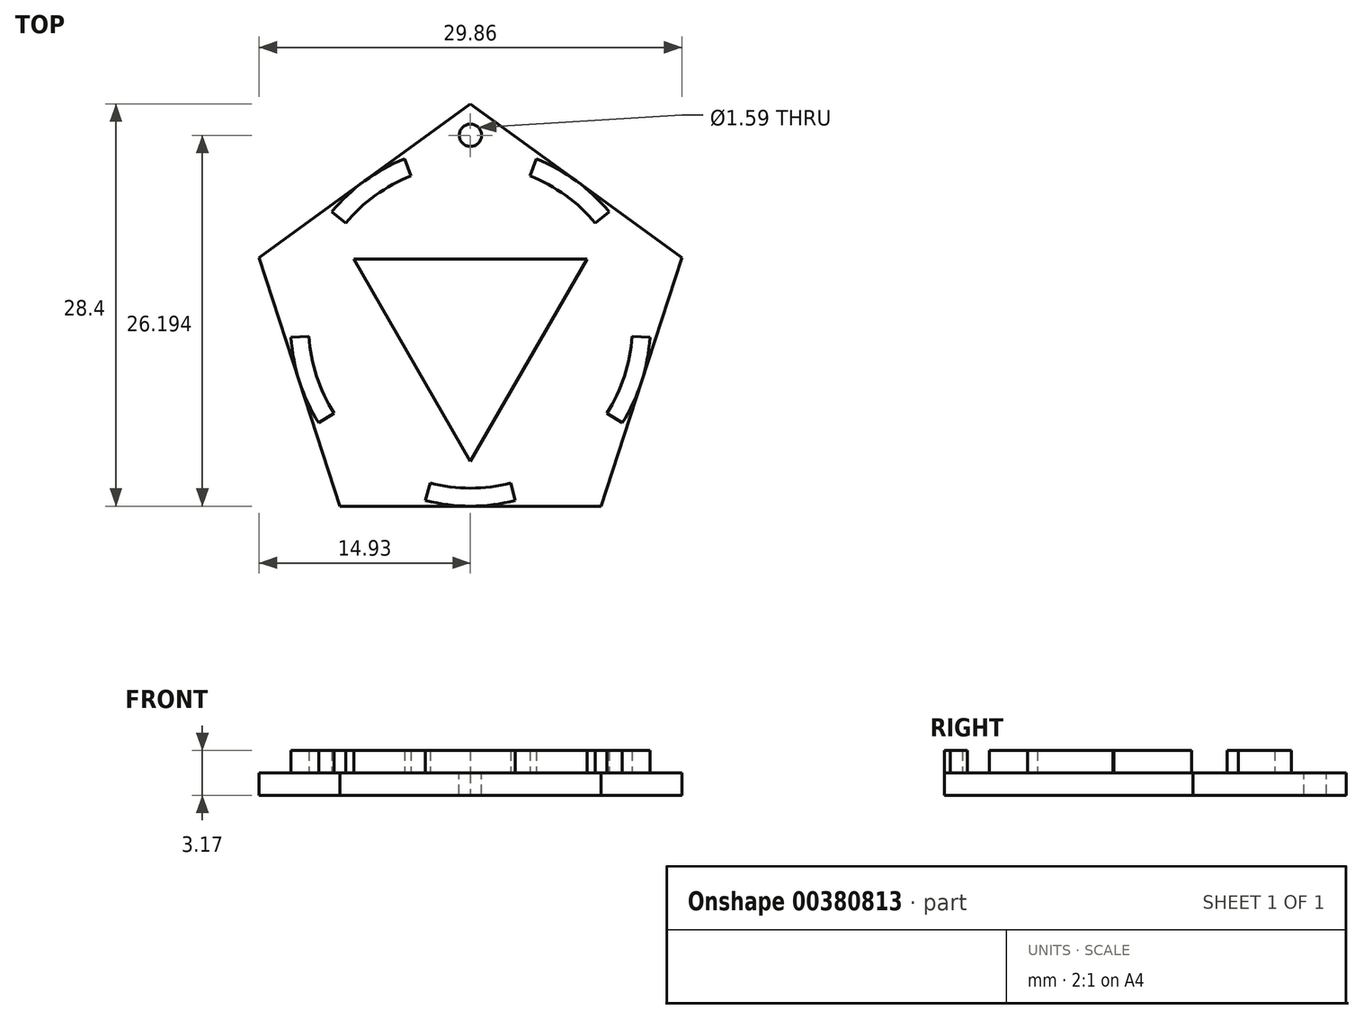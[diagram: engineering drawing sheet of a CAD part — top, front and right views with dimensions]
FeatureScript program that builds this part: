
annotation { "Feature Type Name" : "Feature", "Feature Type Description" : "" }
export const myFeature = defineFeature(function(context is Context, id is Id, definition is map)
    precondition{}
    {
        {
            var Q0;
            Q0=qCreatedBy(makeId("Top.planeOp"),FACE);
            var sketch = newSketch(context, id + "F0", { "sketchPlane" : qUnion([Q0])});
            skCircle(sketch, "E0.cCircle", {"center": v(0, 0) * mm, "radius": 12.7 * mm, "construction": true});
            skLineSegment(sketch, "E0.0", {"start": v(-9.23, -12.7) * mm, "end": v(9.23, -12.7) * mm});
            skLineSegment(sketch, "E0.1", {"start": v(-14.93, 4.85) * mm, "end": v(-9.23, -12.7) * mm});
            skLineSegment(sketch, "E0.2", {"start": v(0, 15.7) * mm, "end": v(-14.93, 4.85) * mm});
            skLineSegment(sketch, "E0.3", {"start": v(14.93, 4.85) * mm, "end": v(0, 15.7) * mm});
            skLineSegment(sketch, "E0.4", {"start": v(9.23, -12.7) * mm, "end": v(14.93, 4.85) * mm});
            skPoint(sketch, "E0.0.midPoint", {"position": v(0, -12.7) * mm});
            skSolve(sketch);
        }
        {
            var Q0;
            Q0 = qSketchRegion(id + "F0", true);
            extrude(context, id + "F1", {"entities" : qUnion([Q0]), "depth" : 1.59 * mm});
        }
        {
            var Q0;
            Q0=makeQuery(id+"F1.opExtrude","CAP_FACE",FACE,{"disambiguationData":[OSD([sQuery(id+"F0.wireOp",EDGE,"E0.0"),sQuery(id+"F0.wireOp",EDGE,"E0.1"),sQuery(id+"F0.wireOp",EDGE,"E0.2"),sQuery(id+"F0.wireOp",EDGE,"E0.3"),sQuery(id+"F0.wireOp",EDGE,"E0.4")])],"isStart":false});
            var sketch = newSketch(context, id + "F2", { "sketchPlane" : qUnion([Q0])});
            skArc(sketch, "E1", {"start": v(-12.68, -0.78) * mm, "mid": v(-12.08, -3.92) * mm, "end": v(-10.71, -6.82) * mm});
            skArc(sketch, "E2", {"start": v(-11.4, -0.71) * mm, "mid": v(-10.87, -3.53) * mm, "end": v(-9.65, -6.13) * mm});
            skLineSegment(sketch, "E3", {"start": v(-7.46, 10.27) * mm, "end": v(-6.72, 9.25) * mm});
            skPoint(sketch, "E4", {"position": v(-7.46, 10.27) * mm});
            skPoint(sketch, "E5", {"position": v(7.46, 10.27) * mm});
            skPoint(sketch, "E6", {"position": v(12.08, -3.92) * mm});
            skPoint(sketch, "E7", {"position": v(0, -12.7) * mm});
            skPoint(sketch, "E8", {"position": v(-12.08, -3.92) * mm});
            skLineSegment(sketch, "E9", {"start": v(-12.08, -3.92) * mm, "end": v(-10.87, -3.53) * mm});
            skLineSegment(sketch, "E10", {"start": v(0, -12.7) * mm, "end": v(0, -11.43) * mm});
            skLineSegment(sketch, "E11", {"start": v(12.08, -3.92) * mm, "end": v(10.87, -3.53) * mm});
            skLineSegment(sketch, "E12", {"start": v(7.46, 10.27) * mm, "end": v(6.72, 9.25) * mm});
            skLineSegment(sketch, "E13", {"start": v(-10.71, -6.82) * mm, "end": v(-9.65, -6.13) * mm});
            skLineSegment(sketch, "E14", {"start": v(-12.68, -0.78) * mm, "end": v(-11.4, -0.71) * mm});
            skLineSegment(sketch, "E15.1.0", {"start": v(-3.17, -12.3) * mm, "end": v(-2.85, -11.07) * mm});
            skLineSegment(sketch, "E15.1.1", {"start": v(3.18, -12.3) * mm, "end": v(2.85, -11.07) * mm});
            skLineSegment(sketch, "E15.2.0", {"start": v(10.71, -6.82) * mm, "end": v(9.65, -6.13) * mm});
            skLineSegment(sketch, "E15.2.1", {"start": v(12.68, -0.78) * mm, "end": v(11.4, -0.71) * mm});
            skLineSegment(sketch, "E15.3.0", {"start": v(9.8, 8.08) * mm, "end": v(8.8, 7.28) * mm});
            skLineSegment(sketch, "E15.3.1", {"start": v(4.66, 11.81) * mm, "end": v(4.2, 10.63) * mm});
            skLineSegment(sketch, "E15.4.0", {"start": v(-4.66, 11.81) * mm, "end": v(-4.2, 10.63) * mm});
            skLineSegment(sketch, "E15.4.1", {"start": v(-9.8, 8.08) * mm, "end": v(-8.8, 7.28) * mm});
            skArc(sketch, "E16.trimOffspring", {"start": v(-4.66, 11.81) * mm, "mid": v(-7.46, 10.27) * mm, "end": v(-9.8, 8.08) * mm});
            skArc(sketch, "E17.trimOffspring", {"start": v(-4.2, 10.63) * mm, "mid": v(-6.72, 9.25) * mm, "end": v(-8.8, 7.28) * mm});
            skArc(sketch, "E18.trimOffspring", {"start": v(8.8, 7.28) * mm, "mid": v(6.72, 9.25) * mm, "end": v(4.2, 10.63) * mm});
            skArc(sketch, "E19.trimOffspring", {"start": v(9.8, 8.08) * mm, "mid": v(7.46, 10.27) * mm, "end": v(4.66, 11.81) * mm});
            skArc(sketch, "E20.trimOffspring", {"start": v(9.65, -6.13) * mm, "mid": v(10.87, -3.53) * mm, "end": v(11.4, -0.71) * mm});
            skArc(sketch, "E21.trimOffspring", {"start": v(10.71, -6.82) * mm, "mid": v(12.08, -3.92) * mm, "end": v(12.68, -0.78) * mm});
            skArc(sketch, "E22.trimOffspring", {"start": v(-3.17, -12.3) * mm, "mid": v(0, -12.7) * mm, "end": v(3.18, -12.3) * mm});
            skArc(sketch, "E23.trimOffspring", {"start": v(-2.85, -11.07) * mm, "mid": v(0, -11.43) * mm, "end": v(2.85, -11.07) * mm});
            skCircle(sketch, "E24.cCircle", {"center": v(0, 0) * mm, "radius": 4.76 * mm, "construction": true});
            skLineSegment(sketch, "E24.0", {"start": v(-8.25, 4.76) * mm, "end": v(8.25, 4.76) * mm});
            skLineSegment(sketch, "E24.1", {"start": v(8.25, 4.76) * mm, "end": v(0, -9.53) * mm});
            skLineSegment(sketch, "E24.2", {"start": v(0, -9.53) * mm, "end": v(-8.25, 4.76) * mm});
            skPoint(sketch, "E24.0.midPoint", {"position": v(0, 4.76) * mm});
            skSolve(sketch);
        }
        {
            var Q0;
            Q0 = qSketchRegion(id + "F2", true);
            extrude(context, id + "F3", {"entities" : qUnion([Q0]), "operationType" : NewBodyOperationType.ADD, "depth" : 1.59 * mm});
        }
        {
            var Q0;
            Q0=makeQuery(id+"F1.opExtrude","CAP_FACE",FACE,{"disambiguationData":[OSD([sQuery(id+"F0.wireOp",EDGE,"E0.0"),sQuery(id+"F0.wireOp",EDGE,"E0.1"),sQuery(id+"F0.wireOp",EDGE,"E0.2"),sQuery(id+"F0.wireOp",EDGE,"E0.3"),sQuery(id+"F0.wireOp",EDGE,"E0.4")])],"isStart":false});
            var sketch = newSketch(context, id + "F4", { "sketchPlane" : qUnion([Q0])});
            skCircle(sketch, "E25", {"center": v(0, 13.5) * mm, "radius": 0.8 * mm});
            skSolve(sketch);
        }
        {
            var Q0;
            Q0 = qSketchRegion(id + "F4", true);
            extrude(context, id + "F5", {"entities" : qUnion([Q0]), "operationType" : NewBodyOperationType.REMOVE, "oppositeDirection" : true, "depth" : 25.4 * mm});
        }
    });
